# Revit family: TP5H - TP5L
name_source: partatom
category: Furniture
revit_build: Autodesk Revit 2016 (Build: 20161004_0715(x64)
units: mm (PartAtom-declared; Revit-internal decimal feet)

## family parameters
Always vertical = Yes
Cut with Voids When Loaded = No
OmniClass Number = 23.40.20.00
OmniClass Title = General Furniture and Specialties
Room Calculation Point = No
Shared = No
Work Plane-Based = No

## types (4) — shared parameters
Back = GABRIEL Byron_11101
High Surround = GABRIEL Byron_02101
Low Surround = GABRIEL Byron_02101
Manufacturer = Gresham Office Furniture
Model = TAKE OFF PLUS
Product Brochure = https://gof.co.uk
Product Data Specification = https://gof.co.uk
Range = SEATING
Seat = GABRIEL Byron_02101
URL = www.gof.co.uk

## per-type parameters (varying)
| type | Angled Base Frame | Circular Leg Frame | High Surround (Vis) | Low Surround (Vis) |
| TP5L-K | Yes | No | No | Yes |
| TP5H-K | Yes | No | Yes | No |
| TP5H-4 | No | Yes | Yes | No |
| TP5L-4 | No | Yes | No | Yes |

note: column(s) folded — value = type name in every type: Product Code

## geometry (parser evidence)
native form markers: Sweep x12
no freeform markers — native parametric forms only
